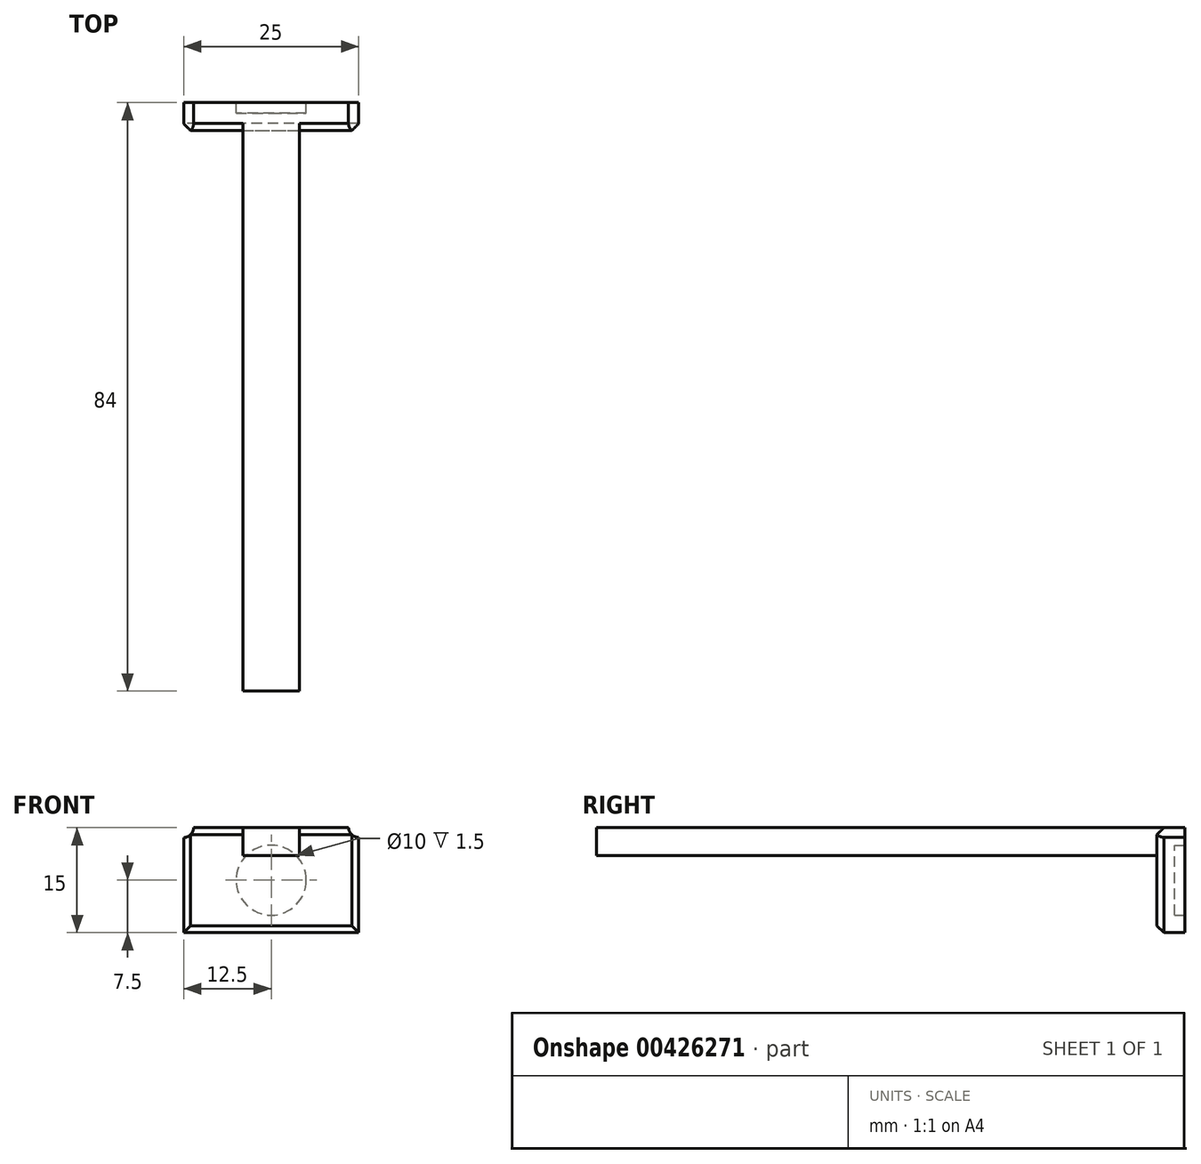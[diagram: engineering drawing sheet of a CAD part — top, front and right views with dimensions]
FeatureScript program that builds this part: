
annotation { "Feature Type Name" : "Feature", "Feature Type Description" : "" }
export const myFeature = defineFeature(function(context is Context, id is Id, definition is map)
    precondition{}
    {
        {
            var Q0;
            Q0=qCreatedBy(makeId("Front.planeOp"),FACE);
            var sketch = newSketch(context, id + "F0", { "sketchPlane" : qUnion([Q0])});
            skLineSegment(sketch, "E0.bottom", {"start": v(-12.5, 7.5) * mm, "end": v(12.5, 7.5) * mm});
            skLineSegment(sketch, "E0.top", {"start": v(-12.5, -7.5) * mm, "end": v(12.5, -7.5) * mm});
            skLineSegment(sketch, "E0.left", {"start": v(-12.5, 7.5) * mm, "end": v(-12.5, -7.5) * mm});
            skLineSegment(sketch, "E0.right", {"start": v(12.5, 7.5) * mm, "end": v(12.5, -7.5) * mm});
            skPoint(sketch, "E0.middle", {"position": v(0, 0) * mm});
            skSolve(sketch);
        }
        {
            var Q0;
            Q0=makeQuery(id+"F0.imprint","IMPRINT",FACE,{"disambiguationData":[TD([[makeQuery(id+"F0.imprint","IMPRINT",EDGE,{"derivedFrom":sQuery(id+"F0.wireOp",EDGE,"E0.bottom")}),-1.0]])]});
            extrude(context, id + "F1", {"entities" : qUnion([Q0]), "depth" : 4 * mm});
        }
        {
            var Q0;
            Q0=qCreatedBy(makeId("Front.planeOp"),FACE);
            var sketch = newSketch(context, id + "F2", { "sketchPlane" : qUnion([Q0])});
            skCircle(sketch, "E1", {"center": v(0, 0) * mm, "radius": 5 * mm});
            skSolve(sketch);
        }
        {
            var Q0;
            Q0=makeQuery(id+"F2.imprint","IMPRINT",FACE,{"disambiguationData":[TD([[makeQuery(id+"F2.imprint","IMPRINT",EDGE,{"derivedFrom":sQuery(id+"F2.wireOp",EDGE,"E1")}),1.0]])]});
            extrude(context, id + "F3", {"entities" : qUnion([Q0]), "operationType" : NewBodyOperationType.REMOVE, "depth" : 1.5 * mm});
        }
        {
            var Q0;
            Q0=makeQuery(id+"F1.opExtrude","CAP_FACE",FACE,{"disambiguationData":[OSD([sQuery(id+"F0.wireOp",EDGE,"E0.bottom"),sQuery(id+"F0.wireOp",EDGE,"E0.top"),sQuery(id+"F0.wireOp",EDGE,"E0.left"),sQuery(id+"F0.wireOp",EDGE,"E0.right")])],"isStart":false});
            var sketch = newSketch(context, id + "F4", { "sketchPlane" : qUnion([Q0])});
            skLineSegment(sketch, "E2", {"start": v(0, 7.5) * mm, "end": v(4, 7.5) * mm});
            skLineSegment(sketch, "E3", {"start": v(0, 7.5) * mm, "end": v(-4, 7.5) * mm});
            skLineSegment(sketch, "E4", {"start": v(-4, 7.5) * mm, "end": v(-4, 3.5) * mm});
            skLineSegment(sketch, "E5", {"start": v(-4, 3.5) * mm, "end": v(4, 3.5) * mm});
            skLineSegment(sketch, "E6", {"start": v(4, 3.5) * mm, "end": v(4, 7.5) * mm});
            skSolve(sketch);
        }
        {
            var Q0;
            Q0=makeQuery(id+"F4.imprint","IMPRINT",FACE,{"disambiguationData":[TD([[makeQuery(id+"F4.imprint","IMPRINT",EDGE,{"derivedFrom":sQuery(id+"F4.wireOp",EDGE,"E2")}),-1.0]])]});
            extrude(context, id + "F5", {"entities" : qUnion([Q0]), "operationType" : NewBodyOperationType.ADD, "depth" : 80 * mm});
        }
        {
            var Q0;
            {var subQ0=sQuery(id+"F0.wireOp",EDGE,"E0.left");var subQ1=sQuery(id+"F0.wireOp",EDGE,"E0.bottom");Q0=makeQuery(id+"F5.boolean.opBoolean","SPLIT",EDGE,{"disambiguationData":[TD([makeQuery(id+"F1.opExtrude","SWEPT_FACE",FACE,{"disambiguationData":[OSD([subQ0])]})])],"derivedFrom":makeQuery(id+"F1.opExtrude","CAP_EDGE",EDGE,{"disambiguationData":[OSD([subQ1])],"isStart":false})});}
            var Q1;
            Q1=makeQuery(id+"F1.opExtrude","CAP_EDGE",EDGE,{"disambiguationData":[OSD([sQuery(id+"F0.wireOp",EDGE,"E0.left")])],"isStart":false});
            var Q2;
            Q2=makeQuery(id+"F1.opExtrude","CAP_EDGE",EDGE,{"disambiguationData":[OSD([sQuery(id+"F0.wireOp",EDGE,"E0.top")])],"isStart":false});
            var Q3;
            Q3=makeQuery(id+"F1.opExtrude","CAP_EDGE",EDGE,{"disambiguationData":[OSD([sQuery(id+"F0.wireOp",EDGE,"E0.right")])],"isStart":false});
            var Q4;
            {var subQ0=sQuery(id+"F0.wireOp",EDGE,"E0.right");var subQ1=sQuery(id+"F0.wireOp",EDGE,"E0.bottom");Q4=makeQuery(id+"F5.boolean.opBoolean","SPLIT",EDGE,{"disambiguationData":[TD([makeQuery(id+"F1.opExtrude","SWEPT_FACE",FACE,{"disambiguationData":[OSD([subQ0])]})])],"derivedFrom":makeQuery(id+"F1.opExtrude","CAP_EDGE",EDGE,{"disambiguationData":[OSD([subQ1])],"isStart":false})});}
            chamfer(context, id + "F6", {"entities" : qUnion([Q0, Q1, Q2, Q3, Q4]), "width" : 1 * mm, "tangentPropagation" : true});
        }
        {
            var Q0;
            Q0=makeQuery(id+"F1.opExtrude","CAP_FACE",FACE,{"disambiguationData":[OSD([sQuery(id+"F0.wireOp",EDGE,"E0.bottom"),sQuery(id+"F0.wireOp",EDGE,"E0.top"),sQuery(id+"F0.wireOp",EDGE,"E0.left"),sQuery(id+"F0.wireOp",EDGE,"E0.right")])],"isStart":false});
            var sketch = newSketch(context, id + "F7", { "sketchPlane" : qUnion([Q0])});
            skCircle(sketch, "E7", {"center": v(-12.51, 7.5) * mm, "radius": 1.42 * mm});
            skCircle(sketch, "E8", {"center": v(12.47, 7.56) * mm, "radius": 1.44 * mm});
            skSolve(sketch);
        }
        {
            var Q0;
            Q0=makeQuery(id+"F7.imprint","IMPRINT",FACE,{"disambiguationData":[TD([[makeQuery(id+"F7.imprint","IMPRINT",EDGE,{"derivedFrom":sQuery(id+"F7.wireOp",EDGE,"E8")}),1.0]])]});
            var Q1;
            Q1=makeQuery(id+"F7.imprint","IMPRINT",FACE,{"disambiguationData":[TD([[makeQuery(id+"F7.imprint","IMPRINT",EDGE,{"derivedFrom":sQuery(id+"F7.wireOp",EDGE,"E7")}),1.0]])]});
            extrude(context, id + "F8", {"entities" : qUnion([Q0, Q1]), "operationType" : NewBodyOperationType.REMOVE, "oppositeDirection" : true, "depth" : 25 * mm});
        }
    });
